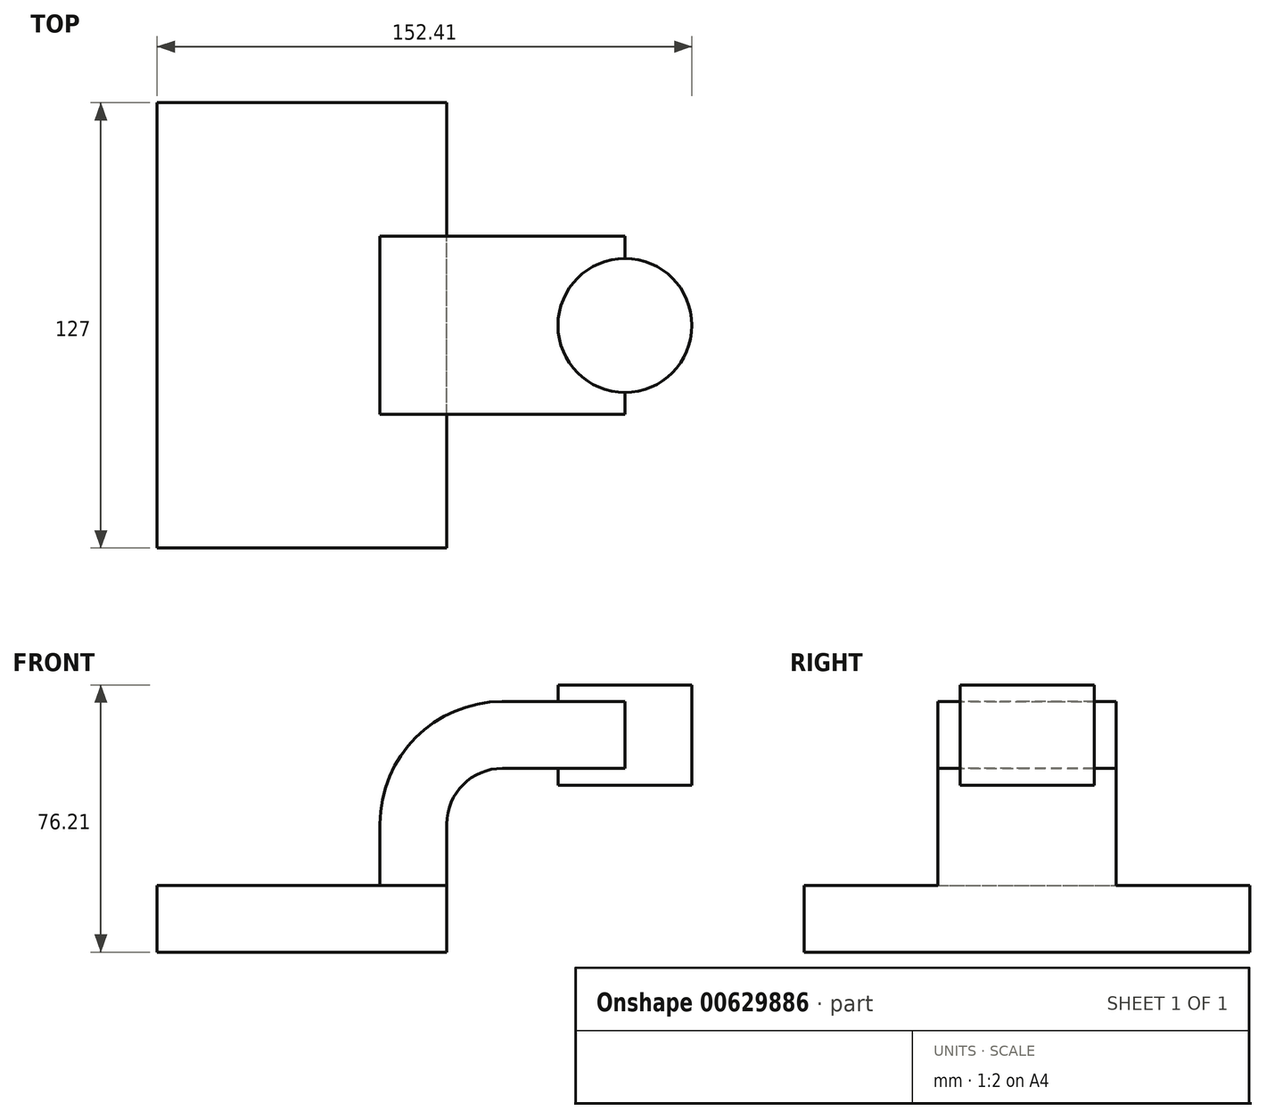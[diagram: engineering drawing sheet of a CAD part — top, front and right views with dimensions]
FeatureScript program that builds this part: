
annotation { "Feature Type Name" : "Feature", "Feature Type Description" : "" }
export const myFeature = defineFeature(function(context is Context, id is Id, definition is map)
    precondition{}
    {
        {
            var Q0;
            Q0=qCreatedBy(makeId("Front.planeOp"),FACE);
            var sketch = newSketch(context, id + "F0", { "sketchPlane" : qUnion([Q0])});
            skLineSegment(sketch, "E0.bottom", {"start": v(41.27, 9.53) * mm, "end": v(-41.28, 9.53) * mm});
            skLineSegment(sketch, "E0.top", {"start": v(41.28, -9.52) * mm, "end": v(-41.27, -9.52) * mm});
            skLineSegment(sketch, "E0.left", {"start": v(41.27, 9.53) * mm, "end": v(41.28, -9.52) * mm});
            skLineSegment(sketch, "E0.right", {"start": v(-41.28, 9.53) * mm, "end": v(-41.27, -9.52) * mm});
            skPoint(sketch, "E0.middle", {"position": v(0, 0) * mm});
            skLineSegment(sketch, "E1.bottom", {"start": v(111.12, 66.68) * mm, "end": v(60.32, 66.68) * mm});
            skLineSegment(sketch, "E1.top", {"start": v(111.12, 38.1) * mm, "end": v(60.32, 38.1) * mm});
            skLineSegment(sketch, "E1.left", {"start": v(111.12, 66.68) * mm, "end": v(111.12, 38.1) * mm});
            skLineSegment(sketch, "E1.right", {"start": v(60.32, 66.68) * mm, "end": v(60.32, 38.1) * mm});
            skPoint(sketch, "E1.middle", {"position": v(85.72, 52.39) * mm});
            skLineSegment(sketch, "E2", {"start": v(41.27, 9.53) * mm, "end": v(41.27, 27) * mm});
            skArc(sketch, "E3", {"start": v(41.27, 27) * mm, "mid": v(45.92, 38.23) * mm, "end": v(57.15, 42.88) * mm});
            skLineSegment(sketch, "E4", {"start": v(57.15, 42.88) * mm, "end": v(92.04, 42.88) * mm});
            skLineSegment(sketch, "E5.0", {"start": v(57.15, 61.93) * mm, "end": v(92.04, 61.93) * mm});
            skArc(sketch, "E5.1", {"start": v(22.22, 27) * mm, "mid": v(32.45, 51.7) * mm, "end": v(57.15, 61.93) * mm});
            skLineSegment(sketch, "E5.2", {"start": v(22.22, 9.53) * mm, "end": v(22.22, 27) * mm});
            skLineSegment(sketch, "E6", {"start": v(92.04, 38.1) * mm, "end": v(92.04, 66.68) * mm});
            skPoint(sketch, "E6.startSnap0", {"position": v(85.72, 38.1) * mm});
            skFitSpline(sketch, "E7", {"points": [v(-41.28, 9.52) * mm, v(57.15, 61.93) * mm], "startDerivative": vector(28.57, 85.74) * mm, "endDerivative": vector(133.96, 0.18) * mm});
            skSolve(sketch);
        }
        {
            var Q0;
            Q0=makeQuery(id+"F0.imprint","IMPRINT",FACE,{"disambiguationData":[TD([[makeQuery(id+"F0.imprint","IMPRINT",EDGE,{"derivedFrom":sQuery(id+"F0.wireOp",EDGE,"E0.top")}),-1.0]])]});
            extrude(context, id + "F1", {"entities" : qUnion([Q0]), "endBound" : BoundingType.SYMMETRIC, "depth" : 127 * mm, "offsetDistance" : 25.4 * mm});
        }
        {
            var Q0;
            {var subQ5=sQuery(id+"F0.wireOp",EDGE,"E2");Q0=makeQuery(id+"F0.imprint","IMPRINT",FACE,{"disambiguationData":[TD([[makeQuery(id+"F0.imprint","IMPRINT",EDGE,{"derivedFrom":subQ5}),1.0]])]});}
            var Q1;
            {var subQ0=sQuery(id+"F0.wireOp",EDGE,"E5.0");var subQ1=sQuery(id+"F0.wireOp",EDGE,"E1.right");var subQ2=makeQuery(id+"F0.imprint","INTERSECT",VERTEX,{"derivedFrom":[subQ1,subQ0]});Q1=makeQuery(id+"F0.imprint","IMPRINT",FACE,{"disambiguationData":[TD([[makeQuery(id+"F0.imprint","IMPRINT",EDGE,{"disambiguationData":[TD([[subQ2,-1.0]])],"derivedFrom":subQ1}),1.0]])]});}
            extrude(context, id + "F2", {"entities" : qUnion([Q0, Q1]), "operationType" : NewBodyOperationType.ADD, "endBound" : BoundingType.SYMMETRIC, "depth" : 50.8 * mm, "offsetDistance" : 25.4 * mm});
        }
        {
            var Q0;
            {var subQ4=sQuery(id+"F0.wireOp",EDGE,"E5.1");Q0=makeQuery(id+"F0.imprint","IMPRINT",FACE,{"disambiguationData":[TD([[makeQuery(id+"F0.imprint","IMPRINT",EDGE,{"derivedFrom":subQ4}),1.0]])]});}
            extrude(context, id + "F3", {"entities" : qUnion([Q0]), "operationType" : NewBodyOperationType.ADD, "endBound" : BoundingType.SYMMETRIC, "depth" : 15.88 * mm, "offsetDistance" : 25.4 * mm});
        }
        {
            var Q0;
            {var subQ4=sQuery(id+"F0.wireOp",EDGE,"E1.left");Q0=makeQuery(id+"F0.imprint","IMPRINT",FACE,{"disambiguationData":[TD([[makeQuery(id+"F0.imprint","IMPRINT",EDGE,{"derivedFrom":subQ4}),-1.0]])]});}
            var Q1;
            Q1=sQuery(id+"F0.wireOp",EDGE,"E6");
            revolve(context, id + "F4", {"operationType" : NewBodyOperationType.ADD, "entities" : qUnion([Q0]), "axis" : qUnion([Q1]), "revolveType" : RevolveType.FULL});
        }
    });
